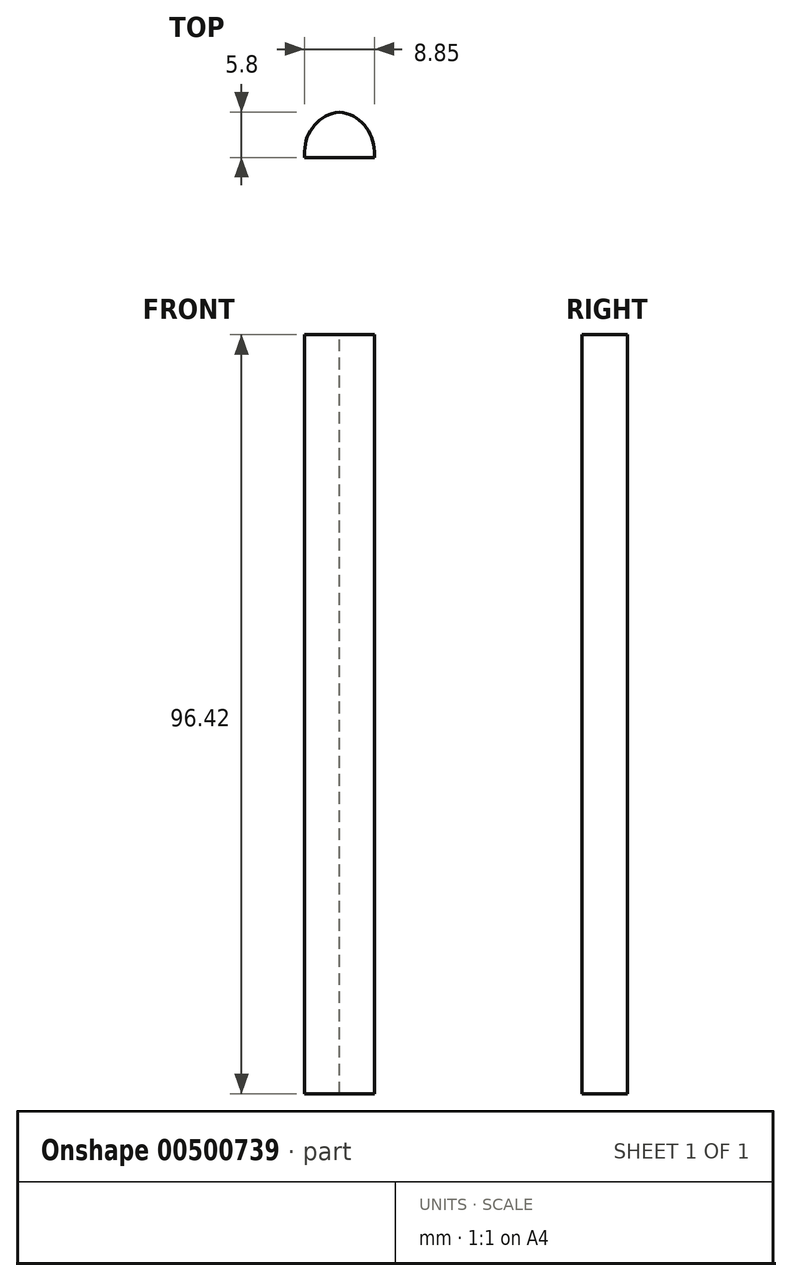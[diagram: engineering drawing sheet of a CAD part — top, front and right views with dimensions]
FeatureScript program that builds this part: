
annotation { "Feature Type Name" : "Feature", "Feature Type Description" : "" }
export const myFeature = defineFeature(function(context is Context, id is Id, definition is map)
    precondition{}
    {
        {
            var Q0;
            Q0=qCreatedBy(makeId("Front.planeOp"),FACE);
            var sketch = newSketch(context, id + "F0", { "sketchPlane" : qUnion([Q0])});
            skLineSegment(sketch, "E0.bottom", {"start": v(-66.92, 45.35) * mm, "end": v(-58.07, 45.35) * mm});
            skLineSegment(sketch, "E0.top", {"start": v(-66.92, -51.07) * mm, "end": v(-58.07, -51.07) * mm});
            skLineSegment(sketch, "E0.left", {"start": v(-66.92, 45.35) * mm, "end": v(-66.92, -51.07) * mm});
            skLineSegment(sketch, "E0.right", {"start": v(-58.07, 45.35) * mm, "end": v(-58.07, -51.07) * mm});
            skSolve(sketch);
        }
        {
            var Q0;
            Q0=makeQuery(id+"F0.imprint","IMPRINT",FACE,{"disambiguationData":[TD([[makeQuery(id+"F0.imprint","IMPRINT",EDGE,{"derivedFrom":sQuery(id+"F0.wireOp",EDGE,"E0.bottom")}),-1.0]])]});
            extrude(context, id + "F1", {"entities" : qUnion([Q0]), "depth" : 5.84 * mm});
        }
        {
            var Q0;
            Q0=makeQuery(id+"F1.opExtrude","CAP_EDGE",EDGE,{"disambiguationData":[OSD([sQuery(id+"F0.wireOp",EDGE,"E0.right")])],"isStart":true});
            var Q1;
            Q1=makeQuery(id+"F1.opExtrude","CAP_EDGE",EDGE,{"disambiguationData":[OSD([sQuery(id+"F0.wireOp",EDGE,"E0.left")])],"isStart":true});
            fillet(context, id + "F2", {"entities" : qUnion([Q0, Q1]), "radius" : 5.08 * mm, "tangentPropagation" : true, "allowEdgeOverflow" : false});
        }
    });
